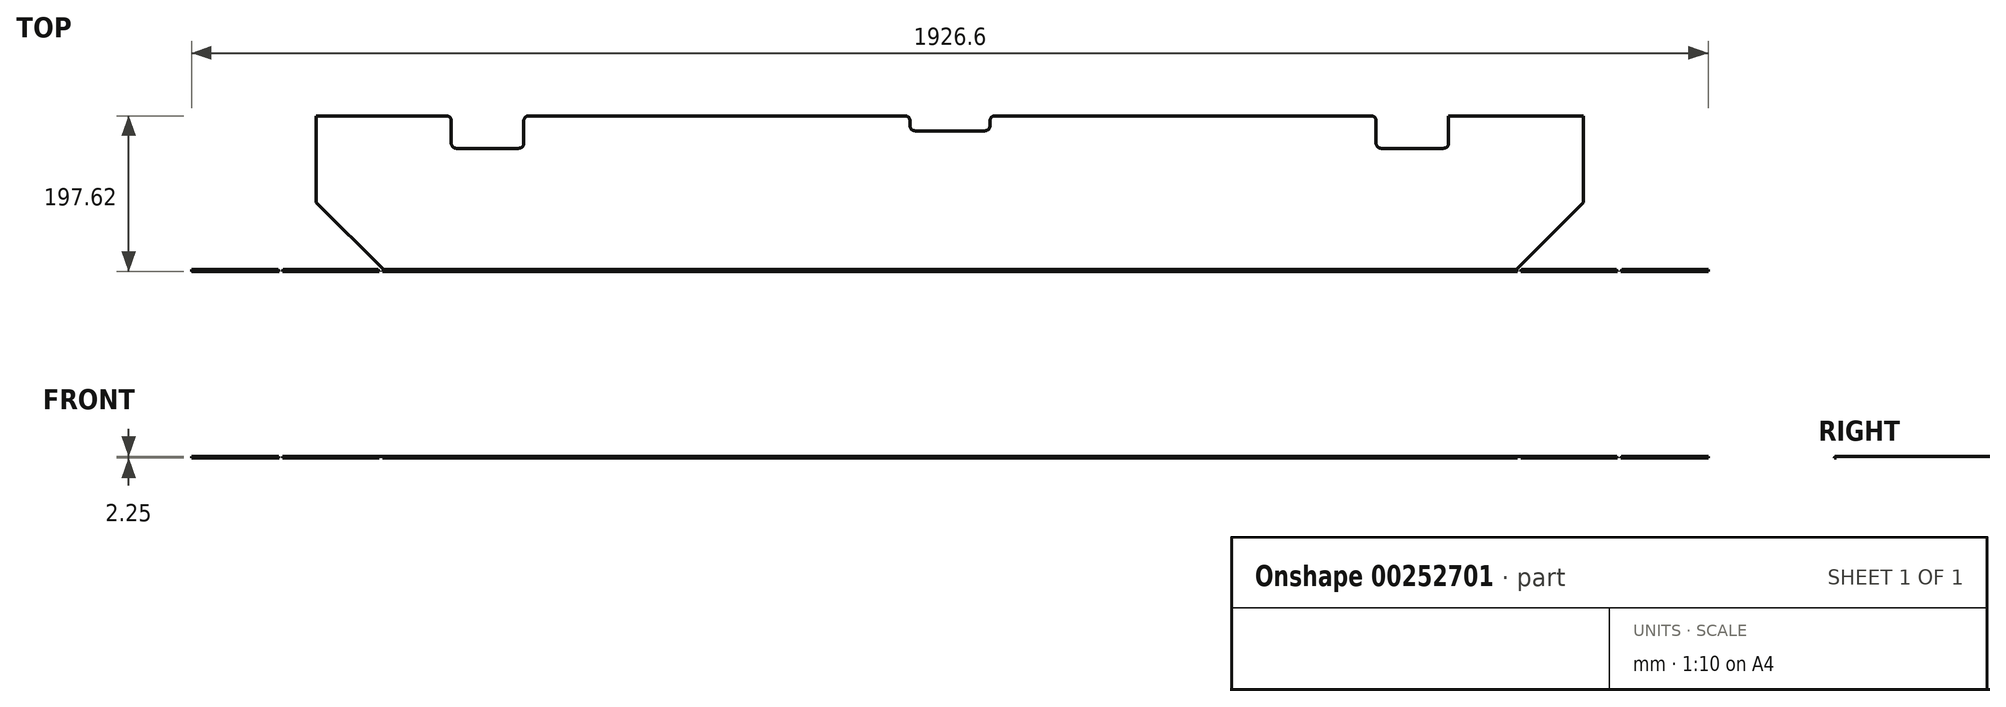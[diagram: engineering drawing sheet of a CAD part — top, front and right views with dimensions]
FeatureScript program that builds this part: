
annotation { "Feature Type Name" : "Feature", "Feature Type Description" : "" }
export const myFeature = defineFeature(function(context is Context, id is Id, definition is map)
    precondition{}
    {
        {
            assignVariable(context, id + "F0", {"name" : "Thickness", "anyValue" : .4});
        }
        {
            assignVariable(context, id + "F1", {"name" : "Height", "anyValue" : 2.25});
        }
        {
            var Q0;
            Q0=qCreatedBy(makeId("Top.planeOp"),FACE);
            var sketch = newSketch(context, id + "F2", { "sketchPlane" : qUnion([Q0])});
            skLineSegment(sketch, "E0.bottom", {"start": v(-804.86, 0) * mm, "end": v(804.86, 0) * mm});
            skLineSegment(sketch, "E0.top", {"start": v(-719.55, -195.26) * mm, "end": v(719.55, -195.26) * mm});
            skLineSegment(sketch, "E0.left", {"start": v(-804.86, 0) * mm, "end": v(-804.86, -109.95) * mm});
            skLineSegment(sketch, "E0.right", {"start": v(804.86, 0) * mm, "end": v(804.86, -109.95) * mm});
            skLineSegment(sketch, "E1", {"start": v(0, 0) * mm, "end": v(0, -68.91) * mm, "construction": true});
            skLineSegment(sketch, "E2", {"start": v(-804.86, -109.95) * mm, "end": v(-719.55, -195.26) * mm});
            skLineSegment(sketch, "E3", {"start": v(719.55, -195.26) * mm, "end": v(804.86, -109.95) * mm});
            skSolve(sketch);
        }
        {
            var Q0;
            Q0 = qSketchRegion(id + "F2", true);
            extrude(context, id + "F3", {"entities" : qUnion([Q0]), "oppositeDirection" : true, "depth" : (getVariable(context, 'Thickness')) * mm});
        }
        {
            var Q0;
            Q0=makeQuery(id+"F3.opExtrude","CAP_FACE",FACE,{"disambiguationData":[OSD([sQuery(id+"F2.wireOp",EDGE,"E0.bottom"),sQuery(id+"F2.wireOp",EDGE,"E0.top"),sQuery(id+"F2.wireOp",EDGE,"E0.left"),sQuery(id+"F2.wireOp",EDGE,"E0.right"),sQuery(id+"F2.wireOp",EDGE,"E2"),sQuery(id+"F2.wireOp",EDGE,"E3")])],"isStart":true});
            var sketch = newSketch(context, id + "F4", { "sketchPlane" : qUnion([Q0])});
            skLineSegment(sketch, "E4.bottom", {"start": v(-1016, -195.26) * mm, "end": v(1016, -195.26) * mm});
            skLineSegment(sketch, "E4.top", {"start": v(-1016, -203.2) * mm, "end": v(1016, -203.2) * mm});
            skLineSegment(sketch, "E4.left", {"start": v(-1016, -195.26) * mm, "end": v(-1016, -203.2) * mm});
            skLineSegment(sketch, "E4.right", {"start": v(1016, -195.26) * mm, "end": v(1016, -203.2) * mm});
            skSolve(sketch);
        }
        {
            var Q0;
            Q0 = qSketchRegion(id + "F4", true);
            extrude(context, id + "F5", {"entities" : qUnion([Q0]), "oppositeDirection" : true, "depth" : (getVariable(context, 'Height')) * mm});
        }
        {
            var Q0;
            Q0=qCreatedBy(makeId("Right.planeOp"),FACE);
            var sketch = newSketch(context, id + "F6", { "sketchPlane" : qUnion([Q0])});
            skLineSegment(sketch, "E5", {"start": v(-201.7, -12.7) * mm, "end": v(-203.2, -12.7) * mm});
            skLineSegment(sketch, "E6", {"start": v(-203.2, -12.7) * mm, "end": v(-203.2, 0) * mm});
            skLineSegment(sketch, "E7", {"start": v(-203.2, 0) * mm, "end": v(-196.76, 0) * mm});
            skFitSpline(sketch, "E8", {"points": [v(-196.76, 0) * mm, v(-197.11, -1.19) * mm, v(-198.68, -4.36) * mm, v(-201.7, -12.7) * mm], "startDerivative": vector(-0.84, -6.12) * mm, "endDerivative": vector(-0.41, -10.99) * mm});
            skSolve(sketch);
        }
        {
            var Q0;
            Q0 = qSketchRegion(id + "F6", true);
            extrude(context, id + "F7", {"entities" : qUnion([Q0]), "operationType" : NewBodyOperationType.REMOVE, "endBound" : BoundingType.THROUGH_ALL, "oppositeDirection" : true, "depth" : 25.4 * mm, "hasSecondDirection" : true, "secondDirectionBound" : SecondDirectionBoundingType.THROUGH_ALL, "secondDirectionOppositeDirection" : false, "secondDirectionDepth" : 25.4 * mm});
        }
        {
            var Q0;
            Q0=makeQuery(id+"F5.opExtrude","SWEPT_FACE",FACE,{"disambiguationData":[OSD([sQuery(id+"F4.wireOp",EDGE,"E4.right")])]});
            var sketch = newSketch(context, id + "F8", { "sketchPlane" : qUnion([Q0])});
            skLineSegment(sketch, "E9.bottom", {"start": v(-203.2, -57.15) * mm, "end": v(-195.26, -57.15) * mm});
            skLineSegment(sketch, "E9.top", {"start": v(-203.2, -31.75) * mm, "end": v(-195.26, -31.75) * mm});
            skLineSegment(sketch, "E9.left", {"start": v(-203.2, -57.15) * mm, "end": v(-203.2, -31.75) * mm});
            skLineSegment(sketch, "E9.right", {"start": v(-195.26, -57.15) * mm, "end": v(-195.26, -31.75) * mm});
            skSolve(sketch);
        }
        {
            var Q0;
            Q0 = qSketchRegion(id + "F8", true);
            extrude(context, id + "F9", {"entities" : qUnion([Q0]), "operationType" : NewBodyOperationType.REMOVE, "endBound" : BoundingType.THROUGH_ALL, "oppositeDirection" : true, "depth" : 25.4 * mm});
        }
        {
            var Q0;
            Q0=makeQuery(id+"F5.opExtrude","CAP_FACE",FACE,{"disambiguationData":[OSD([sQuery(id+"F4.wireOp",EDGE,"E4.bottom"),sQuery(id+"F4.wireOp",EDGE,"E4.top"),sQuery(id+"F4.wireOp",EDGE,"E4.left"),sQuery(id+"F4.wireOp",EDGE,"E4.right")])],"isStart":true});
            var sketch = newSketch(context, id + "F10", { "sketchPlane" : qUnion([Q0])});
            skLineSegment(sketch, "E10", {"start": v(-719.55, -195.26) * mm, "end": v(-722.84, -203.2) * mm});
            skLineSegment(sketch, "E11", {"start": v(-722.84, -203.2) * mm, "end": v(-726.13, -195.26) * mm});
            skLineSegment(sketch, "E12", {"start": v(-726.13, -195.26) * mm, "end": v(-719.55, -195.26) * mm});
            skLineSegment(sketch, "E13", {"start": v(-722.84, -203.2) * mm, "end": v(-722.84, -195.26) * mm, "construction": true});
            skPoint(sketch, "E13.endSnap0", {"position": v(-722.84, -195.26) * mm});
            skLineSegment(sketch, "E14", {"start": v(-846.78, -195.26) * mm, "end": v(-850.06, -203.2) * mm});
            skLineSegment(sketch, "E15", {"start": v(-850.06, -203.2) * mm, "end": v(-853.35, -195.26) * mm});
            skLineSegment(sketch, "E16", {"start": v(-853.35, -195.26) * mm, "end": v(-846.78, -195.26) * mm});
            skLineSegment(sketch, "E17", {"start": v(-850.06, -203.2) * mm, "end": v(-850.06, -195.26) * mm, "construction": true});
            skPoint(sketch, "E17.endSnap0", {"position": v(-850.06, -195.26) * mm});
            skLineSegment(sketch, "E18", {"start": v(0, 0) * mm, "end": v(0, -289.87) * mm, "construction": true});
            skLineSegment(sketch, "E19.MirrorCS", {"start": v(719.55, -195.26) * mm, "end": v(722.84, -203.2) * mm});
            skLineSegment(sketch, "E20.MirrorCS", {"start": v(722.84, -203.2) * mm, "end": v(726.13, -195.26) * mm});
            skLineSegment(sketch, "E21.MirrorCS", {"start": v(722.84, -203.2) * mm, "end": v(722.84, -195.26) * mm, "construction": true});
            skLineSegment(sketch, "E22.MirrorCS", {"start": v(726.13, -195.26) * mm, "end": v(719.55, -195.26) * mm});
            skLineSegment(sketch, "E23.MirrorCS", {"start": v(846.78, -195.26) * mm, "end": v(850.06, -203.2) * mm});
            skLineSegment(sketch, "E24.MirrorCS", {"start": v(850.06, -203.2) * mm, "end": v(853.35, -195.26) * mm});
            skLineSegment(sketch, "E25.MirrorCS", {"start": v(853.35, -195.26) * mm, "end": v(846.78, -195.26) * mm});
            skLineSegment(sketch, "E26.MirrorCS", {"start": v(850.06, -203.2) * mm, "end": v(850.06, -195.26) * mm, "construction": true});
            skPoint(sketch, "E27.MirrorP", {"position": v(722.84, -195.26) * mm});
            skPoint(sketch, "E28.MirrorP", {"position": v(850.06, -195.26) * mm});
            skLineSegment(sketch, "E29.bottom", {"start": v(-1016, -195.26) * mm, "end": v(-963.3, -195.26) * mm});
            skLineSegment(sketch, "E29.top", {"start": v(-1016, -203.2) * mm, "end": v(-963.3, -203.2) * mm});
            skLineSegment(sketch, "E29.left", {"start": v(-1016, -195.26) * mm, "end": v(-1016, -203.2) * mm});
            skLineSegment(sketch, "E29.right", {"start": v(-963.3, -195.26) * mm, "end": v(-963.3, -203.2) * mm});
            skLineSegment(sketch, "E30.MirrorCS", {"start": v(1016, -195.26) * mm, "end": v(1016, -203.2) * mm});
            skLineSegment(sketch, "E31.MirrorCS", {"start": v(963.3, -195.26) * mm, "end": v(963.3, -203.2) * mm});
            skLineSegment(sketch, "E32.MirrorCS", {"start": v(1016, -203.2) * mm, "end": v(963.3, -203.2) * mm});
            skLineSegment(sketch, "E33.MirrorCS", {"start": v(1016, -195.26) * mm, "end": v(963.3, -195.26) * mm});
            skSolve(sketch);
        }
        {
            var Q0;
            Q0 = qSketchRegion(id + "F10", true);
            extrude(context, id + "F11", {"entities" : qUnion([Q0]), "operationType" : NewBodyOperationType.REMOVE, "endBound" : BoundingType.THROUGH_ALL, "oppositeDirection" : true, "depth" : 25.4 * mm});
        }
        {
            var Q0;
            Q0=makeQuery(id+"F3.opExtrude","CAP_FACE",FACE,{"disambiguationData":[OSD([sQuery(id+"F2.wireOp",EDGE,"E0.bottom"),sQuery(id+"F2.wireOp",EDGE,"E0.top"),sQuery(id+"F2.wireOp",EDGE,"E0.left"),sQuery(id+"F2.wireOp",EDGE,"E0.right"),sQuery(id+"F2.wireOp",EDGE,"E2"),sQuery(id+"F2.wireOp",EDGE,"E3")])],"isStart":true});
            var sketch = newSketch(context, id + "F12", { "sketchPlane" : qUnion([Q0])});
            skLineSegment(sketch, "E34", {"start": v(0, 0) * mm, "end": v(0, -195.26) * mm, "construction": true});
            skLineSegment(sketch, "E35.bottom", {"start": v(-633.41, 0) * mm, "end": v(-541.34, 0) * mm});
            skLineSegment(sketch, "E35.top", {"start": v(-633.41, -41.28) * mm, "end": v(-541.34, -41.28) * mm});
            skLineSegment(sketch, "E35.left", {"start": v(-541.34, 0) * mm, "end": v(-541.34, -41.27) * mm});
            skLineSegment(sketch, "E35.right", {"start": v(-633.41, 0) * mm, "end": v(-633.41, -41.27) * mm});
            skLineSegment(sketch, "E36.bottom", {"start": v(-50.8, 0) * mm, "end": v(50.8, 0) * mm});
            skLineSegment(sketch, "E36.top", {"start": v(-50.8, -19.05) * mm, "end": v(50.8, -19.05) * mm});
            skLineSegment(sketch, "E36.left", {"start": v(-50.8, 0) * mm, "end": v(-50.8, -19.05) * mm});
            skLineSegment(sketch, "E36.right", {"start": v(50.8, 0) * mm, "end": v(50.8, -19.05) * mm});
            skLineSegment(sketch, "E37.MirrorCS", {"start": v(633.41, 0) * mm, "end": v(633.41, -41.27) * mm});
            skLineSegment(sketch, "E38.MirrorCS", {"start": v(633.41, -41.28) * mm, "end": v(541.34, -41.28) * mm});
            skLineSegment(sketch, "E39.MirrorCS", {"start": v(633.41, 0) * mm, "end": v(541.34, 0) * mm});
            skLineSegment(sketch, "E40.MirrorCS", {"start": v(541.34, 0) * mm, "end": v(541.34, -41.27) * mm});
            skLineSegment(sketch, "E41", {"start": v(-587.38, -146.35) * mm, "end": v(-587.38, -41.27) * mm, "construction": true});
            skSolve(sketch);
        }
        {
            var Q0;
            Q0 = qSketchRegion(id + "F12", true);
            extrude(context, id + "F13", {"entities" : qUnion([Q0]), "operationType" : NewBodyOperationType.REMOVE, "endBound" : BoundingType.THROUGH_ALL, "oppositeDirection" : true, "depth" : 25.4 * mm});
        }
        {
            var Q0;
            Q0=makeQuery(id+"F13.boolean.opBoolean","COPY",EDGE,{"derivedFrom":makeQuery(id+"F13.opExtrude","SWEPT_EDGE",EDGE,{"disambiguationData":[OSD([sQuery(id+"F2.wireOp",EDGE,"E0.bottom"),sQuery(id+"F12.wireOp",EDGE,"E35.bottom"),sQuery(id+"F12.wireOp",EDGE,"E35.right")])]})});
            var Q1;
            Q1=makeQuery(id+"F13.boolean.opBoolean","COPY",EDGE,{"derivedFrom":makeQuery(id+"F13.opExtrude","SWEPT_EDGE",EDGE,{"disambiguationData":[OSD([sQuery(id+"F12.wireOp",EDGE,"E35.top"),sQuery(id+"F12.wireOp",EDGE,"E35.right")])]})});
            var Q2;
            Q2=makeQuery(id+"F13.boolean.opBoolean","COPY",EDGE,{"derivedFrom":makeQuery(id+"F13.opExtrude","SWEPT_EDGE",EDGE,{"disambiguationData":[OSD([sQuery(id+"F12.wireOp",EDGE,"E35.top"),sQuery(id+"F12.wireOp",EDGE,"E35.left")])]})});
            var Q3;
            Q3=makeQuery(id+"F13.boolean.opBoolean","COPY",EDGE,{"derivedFrom":makeQuery(id+"F13.opExtrude","SWEPT_EDGE",EDGE,{"disambiguationData":[OSD([sQuery(id+"F2.wireOp",EDGE,"E0.bottom"),sQuery(id+"F12.wireOp",EDGE,"E35.bottom"),sQuery(id+"F12.wireOp",EDGE,"E35.left")])]})});
            var Q4;
            Q4=makeQuery(id+"F13.boolean.opBoolean","COPY",EDGE,{"derivedFrom":makeQuery(id+"F13.opExtrude","SWEPT_EDGE",EDGE,{"disambiguationData":[OSD([sQuery(id+"F12.wireOp",EDGE,"E36.top"),sQuery(id+"F12.wireOp",EDGE,"E36.left")])]})});
            var Q5;
            Q5=makeQuery(id+"F13.boolean.opBoolean","COPY",EDGE,{"derivedFrom":makeQuery(id+"F13.opExtrude","SWEPT_EDGE",EDGE,{"disambiguationData":[OSD([sQuery(id+"F2.wireOp",EDGE,"E0.bottom"),sQuery(id+"F12.wireOp",EDGE,"E36.bottom"),sQuery(id+"F12.wireOp",EDGE,"E36.left")])]})});
            var Q6;
            Q6=makeQuery(id+"F13.boolean.opBoolean","COPY",EDGE,{"derivedFrom":makeQuery(id+"F13.opExtrude","SWEPT_EDGE",EDGE,{"disambiguationData":[OSD([sQuery(id+"F2.wireOp",EDGE,"E0.bottom"),sQuery(id+"F12.wireOp",EDGE,"E36.bottom"),sQuery(id+"F12.wireOp",EDGE,"E36.right")])]})});
            var Q7;
            Q7=makeQuery(id+"F13.boolean.opBoolean","COPY",EDGE,{"derivedFrom":makeQuery(id+"F13.opExtrude","SWEPT_EDGE",EDGE,{"disambiguationData":[OSD([sQuery(id+"F12.wireOp",EDGE,"E36.top"),sQuery(id+"F12.wireOp",EDGE,"E36.right")])]})});
            var Q8;
            Q8=makeQuery(id+"F13.boolean.opBoolean","COPY",EDGE,{"derivedFrom":makeQuery(id+"F13.opExtrude","SWEPT_EDGE",EDGE,{"disambiguationData":[OSD([sQuery(id+"F12.wireOp",EDGE,"E37.MirrorCS"),sQuery(id+"F12.wireOp",EDGE,"E38.MirrorCS")])]})});
            var Q9;
            Q9=makeQuery(id+"F13.boolean.opBoolean","COPY",EDGE,{"derivedFrom":makeQuery(id+"F13.opExtrude","SWEPT_EDGE",EDGE,{"disambiguationData":[OSD([sQuery(id+"F2.wireOp",EDGE,"E0.bottom"),sQuery(id+"F12.wireOp",EDGE,"E37.MirrorCS"),sQuery(id+"F12.wireOp",EDGE,"E39.MirrorCS")])]})});
            var Q10;
            Q10=makeQuery(id+"F13.boolean.opBoolean","COPY",EDGE,{"derivedFrom":makeQuery(id+"F13.opExtrude","SWEPT_EDGE",EDGE,{"disambiguationData":[OSD([sQuery(id+"F12.wireOp",EDGE,"E38.MirrorCS"),sQuery(id+"F12.wireOp",EDGE,"E40.MirrorCS")])]})});
            var Q11;
            Q11=makeQuery(id+"F13.boolean.opBoolean","COPY",EDGE,{"derivedFrom":makeQuery(id+"F13.opExtrude","SWEPT_EDGE",EDGE,{"disambiguationData":[OSD([sQuery(id+"F2.wireOp",EDGE,"E0.bottom"),sQuery(id+"F12.wireOp",EDGE,"E39.MirrorCS"),sQuery(id+"F12.wireOp",EDGE,"E40.MirrorCS")])]})});
            fillet(context, id + "F14", {"entities" : qUnion([Q0, Q1, Q2, Q3, Q4, Q5, Q6, Q7, Q8, Q9, Q10, Q11]), "radius" : 6.35 * mm, "tangentPropagation" : true, "allowEdgeOverflow" : false});
        }
    });
